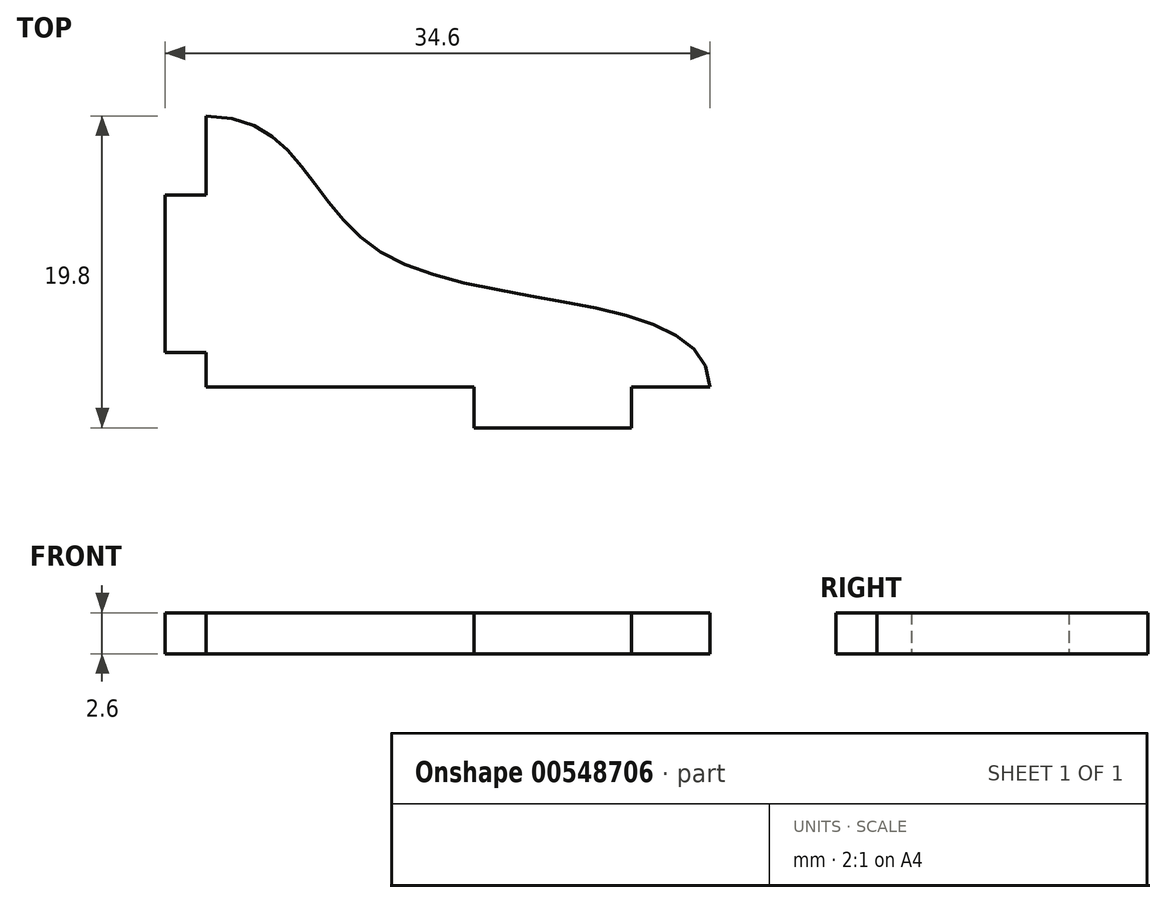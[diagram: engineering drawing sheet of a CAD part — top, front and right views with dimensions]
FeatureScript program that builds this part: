
annotation { "Feature Type Name" : "Feature", "Feature Type Description" : "" }
export const myFeature = defineFeature(function(context is Context, id is Id, definition is map)
    precondition{}
    {
        {
            assignVariable(context, id + "F0", {"variableType" : VariableType.LENGTH, "name" : "MaterialThickness", "lengthValue" : 2.6 * mm});
        }
        {
            var Q0;
            Q0=qCreatedBy(makeId("Top.planeOp"),FACE);
            var sketch = newSketch(context, id + "F1", { "sketchPlane" : qUnion([Q0])});
            skLineSegment(sketch, "E0.bottom", {"start": v(0, 12.2) * mm, "end": v(-2.6, 12.2) * mm});
            skLineSegment(sketch, "E0.top", {"start": v(0, 2.2) * mm, "end": v(-2.6, 2.2) * mm});
            skLineSegment(sketch, "E0.right", {"start": v(-2.6, 12.2) * mm, "end": v(-2.6, 2.2) * mm});
            skLineSegment(sketch, "E1.top", {"start": v(17, -2.6) * mm, "end": v(27, -2.6) * mm});
            skLineSegment(sketch, "E1.left", {"start": v(17, 0) * mm, "end": v(17, -2.6) * mm});
            skLineSegment(sketch, "E1.right", {"start": v(27, 0) * mm, "end": v(27, -2.6) * mm});
            skLineSegment(sketch, "E2", {"start": v(32, 0) * mm, "end": v(32, 0) * mm});
            skLineSegment(sketch, "E3", {"start": v(27, 0) * mm, "end": v(32, 0) * mm});
            skLineSegment(sketch, "E4", {"start": v(17, 0) * mm, "end": v(0, 0) * mm});
            skLineSegment(sketch, "E5", {"start": v(0, 0) * mm, "end": v(0, 2.2) * mm});
            skLineSegment(sketch, "E6", {"start": v(0, 12.2) * mm, "end": v(0, 17.2) * mm});
            skFitSpline(sketch, "E7", {"points": [v(0, 17.2) * mm, v(11.53, 8.31) * mm, v(32, 0) * mm], "startDerivative": vector(41.95, 0.35) * mm, "endDerivative": vector(1, -33.52) * mm});
            skSolve(sketch);
        }
        {
            var Q0;
            Q0=makeQuery(id+"F1.imprint","IMPRINT",FACE,{"disambiguationData":[TD([[makeQuery(id+"F1.imprint","IMPRINT",EDGE,{"derivedFrom":sQuery(id+"F1.wireOp",EDGE,"E0.bottom")}),1.0]])]});
            extrude(context, id + "F2", {"entities" : qUnion([Q0]), "depth" : getVariable(context, 'MaterialThickness') / 2, "offsetDistance" : 25 * mm, "hasSecondDirection" : true, "secondDirectionOppositeDirection" : true, "secondDirectionDepth" : getVariable(context, 'MaterialThickness') / 2});
        }
    });
